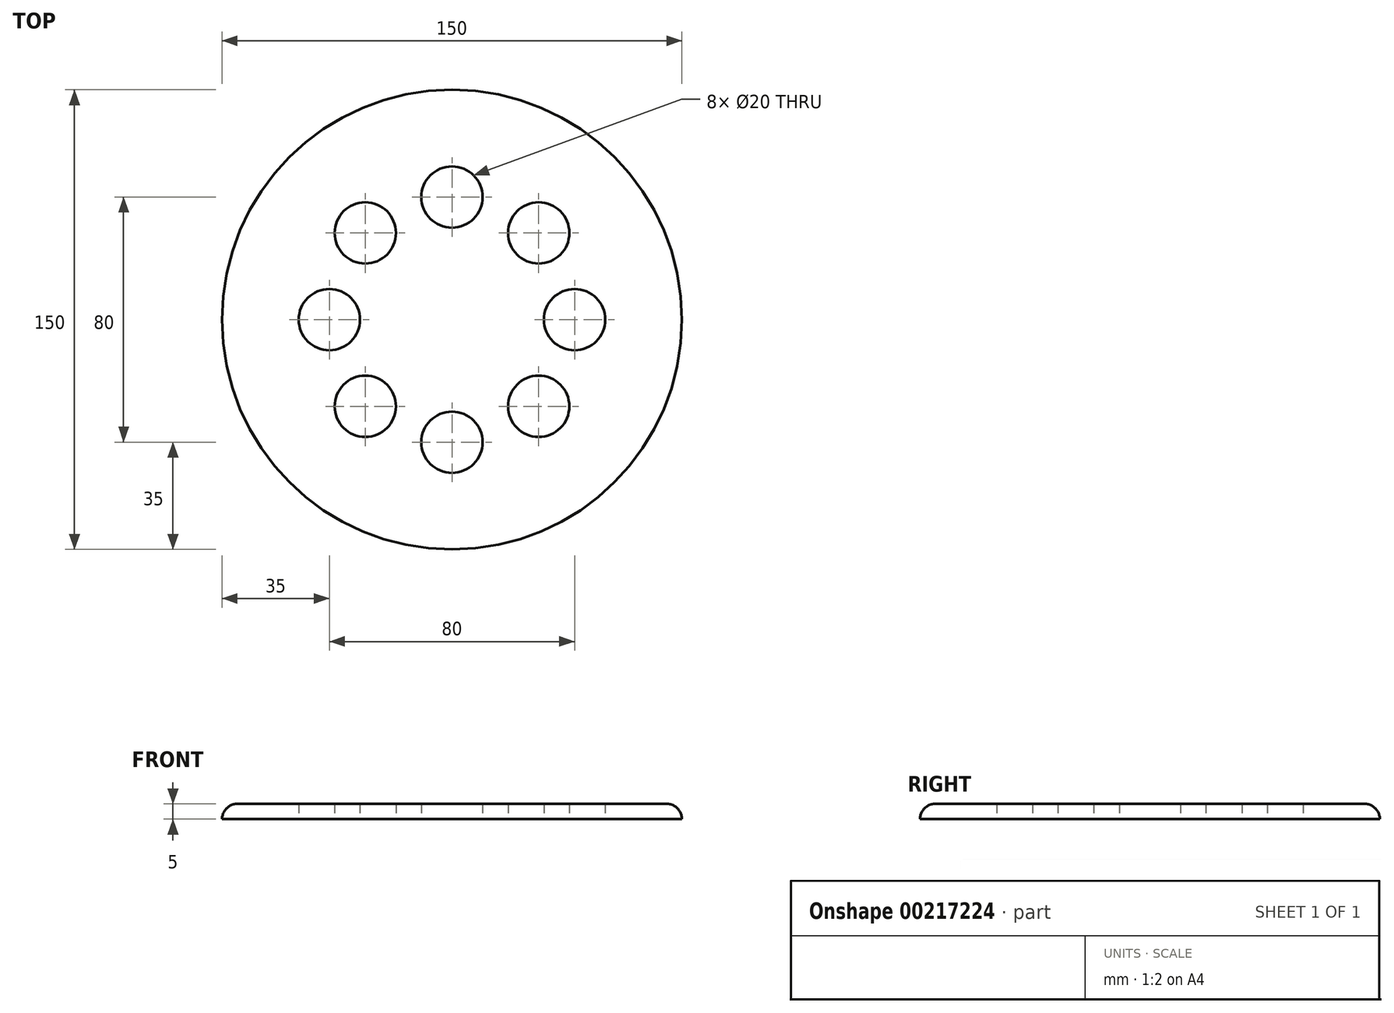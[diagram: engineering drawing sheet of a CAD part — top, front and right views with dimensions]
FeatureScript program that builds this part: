
annotation { "Feature Type Name" : "Feature", "Feature Type Description" : "" }
export const myFeature = defineFeature(function(context is Context, id is Id, definition is map)
    precondition{}
    {
        {
            var Q0;
            Q0=qCreatedBy(makeId("Top.planeOp"),FACE);
            var sketch = newSketch(context, id + "F0", { "sketchPlane" : qUnion([Q0])});
            skCircle(sketch, "E0", {"center": v(0, 0) * mm, "radius": 75 * mm});
            skCircle(sketch, "E1", {"center": v(0, 40) * mm, "radius": 10 * mm});
            skCircle(sketch, "E2.1.0", {"center": v(-28.28, 28.28) * mm, "radius": 10 * mm});
            skCircle(sketch, "E2.2.0", {"center": v(-40, 0) * mm, "radius": 10 * mm});
            skCircle(sketch, "E2.3.0", {"center": v(-28.28, -28.28) * mm, "radius": 10 * mm});
            skCircle(sketch, "E2.4.0", {"center": v(0, -40) * mm, "radius": 10 * mm});
            skCircle(sketch, "E2.5.0", {"center": v(28.28, -28.28) * mm, "radius": 10 * mm});
            skCircle(sketch, "E2.6.0", {"center": v(40, 0) * mm, "radius": 10 * mm});
            skCircle(sketch, "E2.7.0", {"center": v(28.28, 28.28) * mm, "radius": 10 * mm});
            skSolve(sketch);
        }
        {
            var Q0;
            Q0=makeQuery(id+"F0.imprint","IMPRINT",FACE,{"disambiguationData":[TD([[makeQuery(id+"F0.imprint","IMPRINT",EDGE,{"derivedFrom":sQuery(id+"F0.wireOp",EDGE,"E0")}),1.0]])]});
            extrude(context, id + "F1", {"entities" : qUnion([Q0]), "depth" : 5 * mm});
        }
        {
            var Q0;
            Q0=makeQuery(id+"F1.opExtrude","CAP_EDGE",EDGE,{"disambiguationData":[OSD([sQuery(id+"F0.wireOp",EDGE,"E0")])],"isStart":false});
            fillet(context, id + "F2", {"entities" : qUnion([Q0]), "radius" : 5 * mm, "tangentPropagation" : true, "allowEdgeOverflow" : false});
        }
        {
            var Q0;
            Q0=makeQuery(id+"F1.opExtrude","CAP_FACE",FACE,{"disambiguationData":[OSD([sQuery(id+"F0.wireOp",EDGE,"E0"),sQuery(id+"F0.wireOp",EDGE,"E1"),sQuery(id+"F0.wireOp",EDGE,"E2.1.0"),sQuery(id+"F0.wireOp",EDGE,"E2.2.0"),sQuery(id+"F0.wireOp",EDGE,"E2.3.0"),sQuery(id+"F0.wireOp",EDGE,"E2.4.0"),sQuery(id+"F0.wireOp",EDGE,"E2.5.0"),sQuery(id+"F0.wireOp",EDGE,"E2.6.0"),sQuery(id+"F0.wireOp",EDGE,"E2.7.0")])],"isStart":true});
            var sketch = newSketch(context, id + "F3", { "sketchPlane" : qUnion([Q0])});
            skCircle(sketch, "E3", {"center": v(-20.94, 54.08) * mm, "radius": 8.22 * mm});
            skCircle(sketch, "E4.1.0", {"center": v(-54.08, -20.94) * mm, "radius": 8.22 * mm});
            skCircle(sketch, "E4.2.0", {"center": v(20.94, -54.08) * mm, "radius": 8.22 * mm});
            skCircle(sketch, "E4.3.0", {"center": v(54.08, 20.94) * mm, "radius": 8.22 * mm});
            skPoint(sketch, "E4.center", {"position": v(0, 0) * mm});
            skSolve(sketch);
        }
        {
            var Q0;
            Q0=sQuery(id+"F3.wireOp",EDGE,"E3");
            var Q1;
            Q1=sQuery(id+"F3.wireOp",EDGE,"E4.3.0");
            var Q2;
            Q2=sQuery(id+"F3.wireOp",EDGE,"E4.2.0");
            var Q3;
            Q3=sQuery(id+"F3.wireOp",EDGE,"E4.1.0");
            extrude(context, id + "F4", {"bodyType" : ToolBodyType.SURFACE, "surfaceEntities" : qUnion([Q0, Q1, Q2, Q3]), "depth" : 100 * mm});
        }
    });
